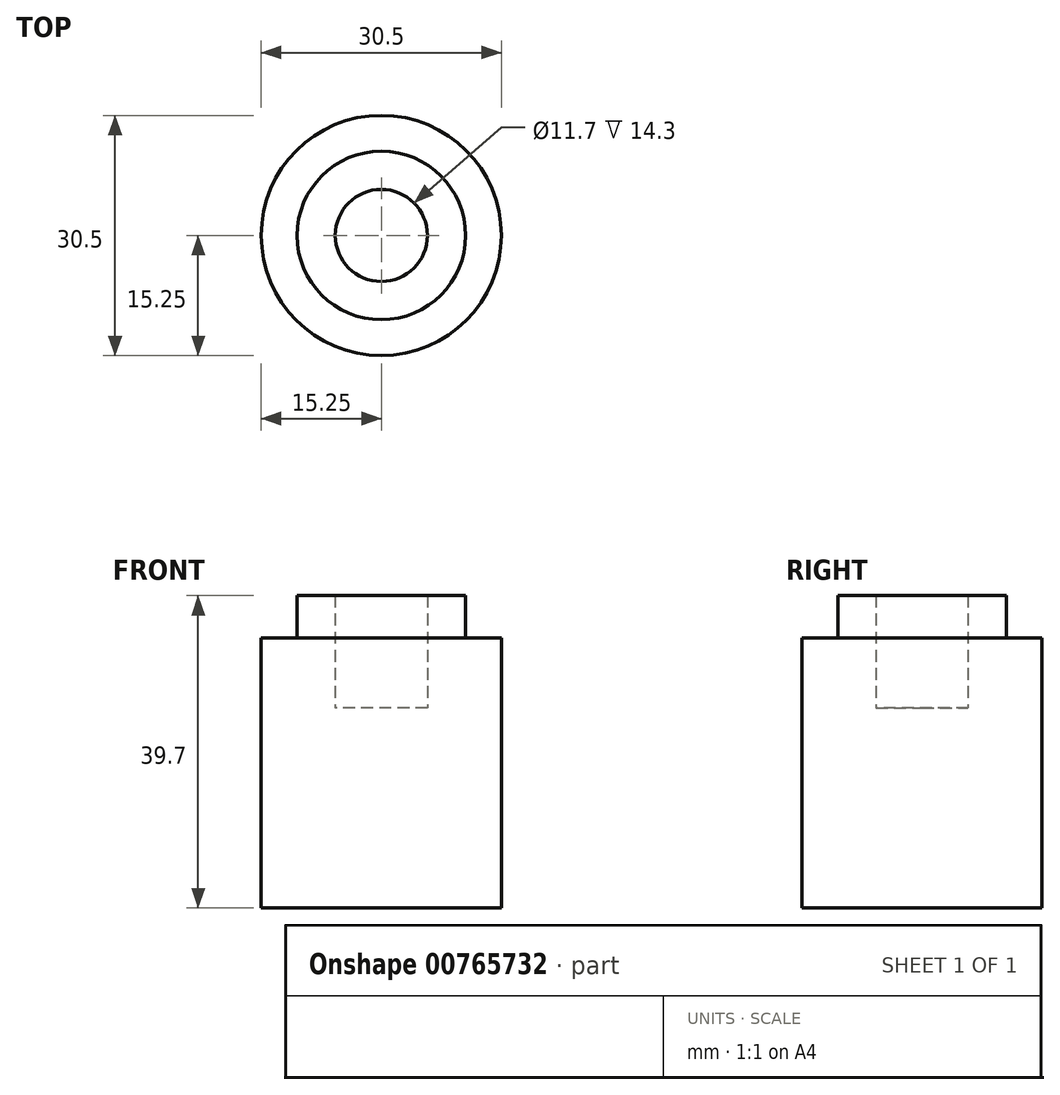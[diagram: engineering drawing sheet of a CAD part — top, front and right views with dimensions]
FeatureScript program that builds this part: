
annotation { "Feature Type Name" : "Feature", "Feature Type Description" : "" }
export const myFeature = defineFeature(function(context is Context, id is Id, definition is map)
    precondition{}
    {
        {
            var Q0;
            Q0=qCreatedBy(makeId("Top.planeOp"),FACE);
            var sketch = newSketch(context, id + "F0", { "sketchPlane" : qUnion([Q0])});
            skCircle(sketch, "E0", {"center": v(0, 0) * mm, "radius": 15.25 * mm});
            skCircle(sketch, "E1", {"center": v(0, 0) * mm, "radius": 5.85 * mm});
            skCircle(sketch, "E2", {"center": v(0, 0) * mm, "radius": 10.7 * mm});
            skSolve(sketch);
        }
        {
            var Q0;
            Q0 = qSketchRegion(id + "F0", true);
            extrude(context, id + "F1", {"entities" : qUnion([Q0]), "depth" : 34.3 * mm, "offsetDistance" : 25.4 * mm});
        }
        {
            var Q0;
            Q0=makeQuery(id+"F0.imprint","IMPRINT",FACE,{"disambiguationData":[TD([[makeQuery(id+"F0.imprint","IMPRINT",EDGE,{"derivedFrom":sQuery(id+"F0.wireOp",EDGE,"E1")}),-1.0]])]});
            extrude(context, id + "F2", {"entities" : qUnion([Q0]), "operationType" : NewBodyOperationType.ADD, "depth" : 39.7 * mm, "offsetDistance" : 25.4 * mm});
        }
        {
            var Q0;
            Q0=makeQuery(id+"F0.imprint","IMPRINT",FACE,{"disambiguationData":[TD([[makeQuery(id+"F0.imprint","IMPRINT",EDGE,{"derivedFrom":sQuery(id+"F0.wireOp",EDGE,"E1")}),1.0]])]});
            extrude(context, id + "F3", {"entities" : qUnion([Q0]), "operationType" : NewBodyOperationType.ADD, "depth" : 25.4 * mm, "offsetDistance" : 25.4 * mm});
        }
    });
